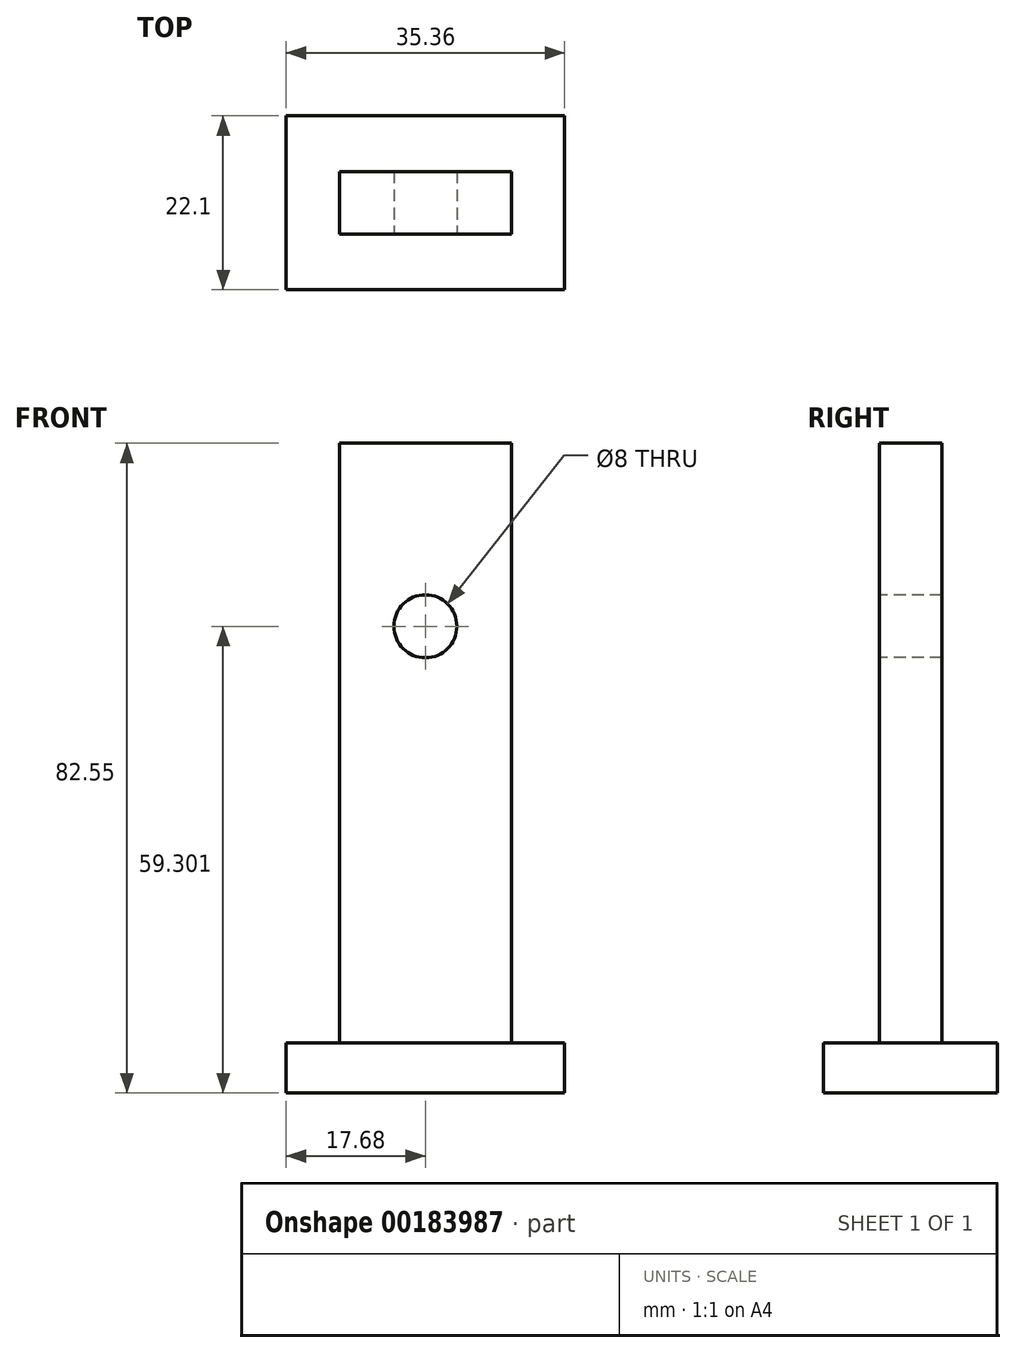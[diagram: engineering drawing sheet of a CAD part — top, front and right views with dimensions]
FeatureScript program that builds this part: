
annotation { "Feature Type Name" : "Feature", "Feature Type Description" : "" }
export const myFeature = defineFeature(function(context is Context, id is Id, definition is map)
    precondition{}
    {
        {
            var Q0;
            Q0=qCreatedBy(makeId("Top.planeOp"),FACE);
            var sketch = newSketch(context, id + "F0", { "sketchPlane" : qUnion([Q0])});
            skLineSegment(sketch, "E0.bottom", {"start": v(17.68, 11.05) * mm, "end": v(-17.68, 11.05) * mm});
            skLineSegment(sketch, "E0.top", {"start": v(17.68, -11.05) * mm, "end": v(-17.68, -11.05) * mm});
            skLineSegment(sketch, "E0.left", {"start": v(17.68, 11.05) * mm, "end": v(17.68, -11.05) * mm});
            skLineSegment(sketch, "E0.right", {"start": v(-17.68, 11.05) * mm, "end": v(-17.68, -11.05) * mm});
            skPoint(sketch, "E0.middle", {"position": v(0, 0) * mm});
            skSolve(sketch);
        }
        {
            var Q0;
            Q0=makeQuery(id+"F0.imprint","IMPRINT",FACE,{"disambiguationData":[TD([[makeQuery(id+"F0.imprint","IMPRINT",EDGE,{"derivedFrom":sQuery(id+"F0.wireOp",EDGE,"E0.bottom")}),1.0]])]});
            extrude(context, id + "F1", {"entities" : qUnion([Q0]), "depth" : 6.35 * mm});
        }
        {
            var Q0;
            Q0=makeQuery(id+"F1.opExtrude","CAP_FACE",FACE,{"disambiguationData":[OSD([sQuery(id+"F0.wireOp",EDGE,"E0.bottom"),sQuery(id+"F0.wireOp",EDGE,"E0.top"),sQuery(id+"F0.wireOp",EDGE,"E0.left"),sQuery(id+"F0.wireOp",EDGE,"E0.right")])],"isStart":false});
            var sketch = newSketch(context, id + "F2", { "sketchPlane" : qUnion([Q0])});
            skLineSegment(sketch, "E1.bottom", {"start": v(10.9, 3.98) * mm, "end": v(-10.9, 3.98) * mm});
            skLineSegment(sketch, "E1.top", {"start": v(10.9, -3.98) * mm, "end": v(-10.9, -3.98) * mm});
            skLineSegment(sketch, "E1.left", {"start": v(10.9, 3.98) * mm, "end": v(10.9, -3.98) * mm});
            skLineSegment(sketch, "E1.right", {"start": v(-10.9, 3.98) * mm, "end": v(-10.9, -3.98) * mm});
            skPoint(sketch, "E1.middle", {"position": v(0, 0) * mm});
            skSolve(sketch);
        }
        {
            var Q0;
            Q0 = qSketchRegion(id + "F2", true);
            extrude(context, id + "F3", {"entities" : qUnion([Q0]), "depth" : 76.2 * mm});
        }
        {
            var Q0;
            Q0=makeQuery(id+"F3.opExtrude","SWEPT_FACE",FACE,{"disambiguationData":[OSD([sQuery(id+"F2.wireOp",EDGE,"E1.top")])]});
            var sketch = newSketch(context, id + "F4", { "sketchPlane" : qUnion([Q0])});
            skCircle(sketch, "E2", {"center": v(0, 59.3) * mm, "radius": 4 * mm});
            skPoint(sketch, "E3", {"position": v(0, 82.55) * mm});
            skSolve(sketch);
        }
        {
            var Q0;
            Q0 = qSketchRegion(id + "F4", true);
            extrude(context, id + "F5", {"entities" : qUnion([Q0]), "operationType" : NewBodyOperationType.REMOVE, "endBound" : BoundingType.THROUGH_ALL, "oppositeDirection" : true, "depth" : 25.4 * mm});
        }
    });
